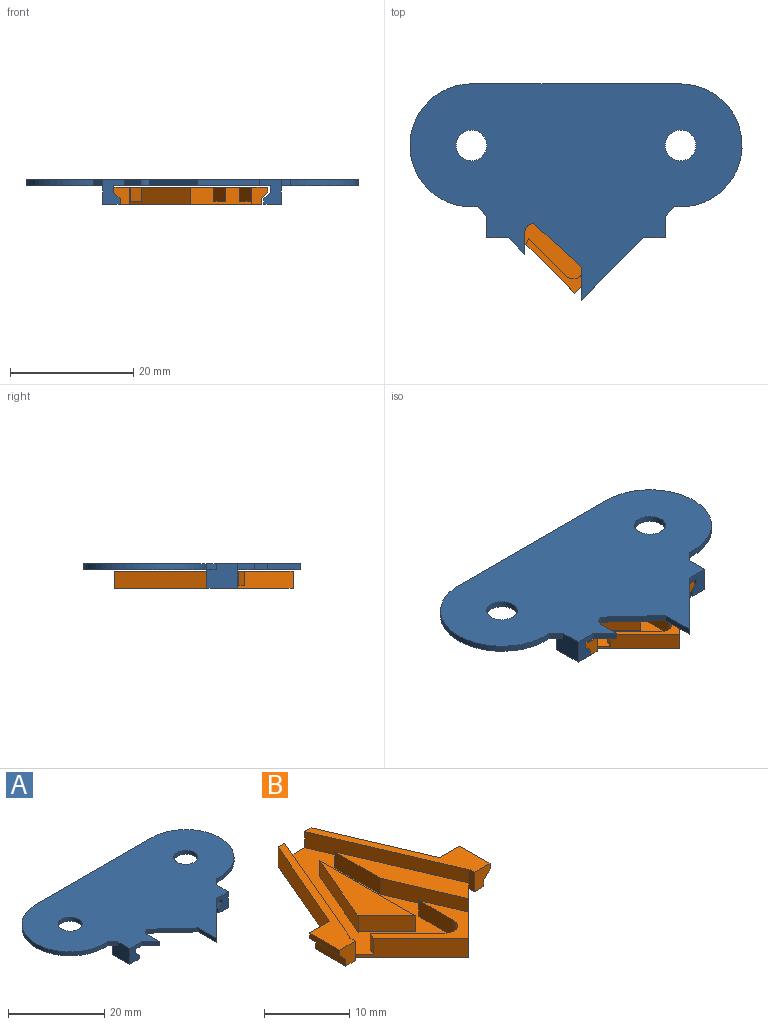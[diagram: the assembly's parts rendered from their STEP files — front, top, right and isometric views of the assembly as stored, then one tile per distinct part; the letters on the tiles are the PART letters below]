
ASSEMBLY  parts=2 mates=1
PART A: 29 faces, bbox 54x35.1x4 mm
  f0: plane 1.54x1.54mm, normal (0.71,-0.71,0), area 2.2mm2, adj f2,f4,f10,f15
  f1: plane 2.69x2.69mm, normal (-0.71,-0.71,0), area 3.8mm2, adj f2,f4,f9,f27
  f2: plane 54x35.14mm, normal (0,0,-1), area 1145.9mm2, adj f0,f1,f3,f5,f6,f7,f8,f9
  f3: plane 1.55x1.55mm, normal (-0.71,-0.71,0), area 2.2mm2, adj f2,f4,f13,f23
  f4: plane 54x35.14mm, normal (0,0,1), area 1163.9mm2, adj f0,f1,f3,f5,f6,f7,f8,f9
  f5: plane 10.14x10.14mm, normal (0.71,-0.71,0), area 14.3mm2, adj f2,f4,f6,f20
  f6: plane 5.36x1mm, normal (-1,0,0), area 5.4mm2, adj f2,f4,f5,f7
  f7: plane 7.7x7.05mm, normal (-0.68,-0.74,0), area 10.4mm2, adj f2,f4,f6,f8
  f8: cylinder r=1.46mm len=1.47mm, axis (0,0,1), area 2.3mm2, adj f2,f4,f7,f9
  f9: plane 3.5x1mm, normal (1,0,0), area 3.5mm2, adj f1,f2,f4,f8
  f10: cylinder r=10mm len=20mm, axis (0,0,1), area 32.4mm2, adj f0,f2,f4,f11
  f11: plane 34.12x1mm, normal (0,1,0), area 34.1mm2, adj f2,f4,f10,f13
  f12: cylinder r=2.5mm len=5mm, axis (0,0,1), area 15.7mm2, adj f2,f4
  f13: cylinder r=10mm len=20mm, axis (0,0,1), area 32.3mm2, adj f2,f3,f4,f11
  f14: cylinder r=2.5mm len=5mm, axis (0,0,1), area 15.7mm2, adj f2,f4
  f15: plane 5x4mm, normal (1,0,0), area 18.5mm2, adj f0,f2,f4,f16,f20,f21
  f16: plane 5x2.8mm, normal (0,0,-1), area 14mm2, adj f15,f17,f20,f21
  f17: plane 5x0.92mm, normal (-1,0,0), area 4.6mm2, adj f16,f18,f20,f21
  f18: plane 5x1mm, normal (-0.71,0,0.71), area 7.1mm2, adj f17,f19,f20,f21
  f19: plane 5x1.08mm, normal (-1,0,0), area 5.4mm2, adj f2,f18,f20,f21
  f20: plane 4x3.5mm, normal (0,-1,0), area 10.3mm2, adj f2,f4,f5,f15,f16,f17,f18,f19
  f21: plane 3x2.8mm, normal (0,1,0), area 6.8mm2, adj f2,f15,f16,f17,f18,f19
  f22: plane 5x2.8mm, normal (0,0,-1), area 14mm2, adj f23,f26,f27,f28
  f23: plane 5x4mm, normal (-1,0,0), area 18.5mm2, adj f2,f3,f4,f22,f27,f28
  f24: plane 5x1.08mm, normal (1,0,0), area 5.4mm2, adj f2,f25,f27,f28
  f25: plane 5x1mm, normal (0.71,0,0.71), area 7.1mm2, adj f24,f26,f27,f28
  f26: plane 5x0.92mm, normal (1,0,0), area 4.6mm2, adj f22,f25,f27,f28
  f27: plane 4x3.5mm, normal (0,-1,0), area 10.3mm2, adj f1,f2,f4,f22,f23,f24,f25,f26
  f28: plane 3x2.8mm, normal (0,1,0), area 6.8mm2, adj f2,f22,f23,f24,f25,f26
PART B: 38 faces, bbox 25x29x2.8 mm
  f0: plane 9.9x9.9mm, normal (-0.71,-0.71,0), area 33mm2, adj f2,f6,f8,f9,f21,f22,f24,f37
  f1: plane 15x6.41mm, normal (0.92,0.39,0), area 45.7mm2, adj f3,f4,f9,f30
  f2: plane 9.9x9.9mm, normal (0.71,-0.71,0), area 26.8mm2, adj f0,f4,f5,f6,f9,f16,f17,f19
  f3: plane 5.5x2.8mm, normal (0,1,0), area 7.8mm2, adj f1,f4,f7,f8,f9,f20,f21,f24
  f4: plane 20x10.84mm, normal (0,0,1), area 33.2mm2, adj f1,f2,f3,f20,f26,f29,f30,f36
  f5: plane 17.95x6.69mm, normal (0,0,1), area 42.4mm2, adj f2,f17,f18,f19
  f6: plane 11.69x9.6mm, normal (0,0,1), area 24.3mm2, adj f0,f2,f13,f14,f15,f16,f22
  f7: plane 15x6.41mm, normal (-0.92,0.39,0), area 45.7mm2, adj f3,f8,f9,f35
  f8: plane 20x10.84mm, normal (0,0,1), area 33.2mm2, adj f0,f3,f7,f21,f32,f34,f35,f37
  f9: plane 29x23mm, normal (0,0,-1), area 373.8mm2, adj f0,f1,f2,f3,f7,f28,f29,f30
  f10: plane 11.29x4.82mm, normal (-0.92,0.39,0), area 28.2mm2, adj f11,f23,f24,f25
  f11: plane 15.99x2.3mm, normal (1,0,0), area 36.8mm2, adj f10,f12,f24,f25
  f12: plane 4.76x4.76mm, normal (-0.71,-0.71,0), area 15.5mm2, adj f11,f23,f24,f25
  f13: plane 6.21x6.21mm, normal (0.71,0.71,0), area 20.2mm2, adj f6,f14,f22,f24
  f14: cylinder r=1.5mm len=2.56mm, axis (0,0,1), area 8.1mm2, adj f6,f13,f15,f24
  f15: plane 5.81x2.3mm, normal (-1,0,0), area 13.4mm2, adj f6,f14,f16,f24
  f16: plane 5.85x2.5mm, normal (0.92,0.39,0), area 14.6mm2, adj f2,f6,f15,f24
  f17: plane 10.31x4.4mm, normal (-0.92,-0.39,0), area 25.8mm2, adj f2,f5,f18,f24
  f18: plane 7.64x2.3mm, normal (-1,0,0), area 17.6mm2, adj f5,f17,f19,f24
  f19: plane 15.66x6.69mm, normal (0.92,0.39,0), area 39.2mm2, adj f2,f5,f18,f24
  f20: plane 19.15x8.18mm, normal (-0.92,-0.39,0), area 47.9mm2, adj f2,f3,f4,f24
  f21: plane 19.15x8.18mm, normal (0.92,-0.39,0), area 47.9mm2, adj f0,f3,f8,f24
  f22: plane 2.3x0.99mm, normal (-0.92,0.39,0), area 2.5mm2, adj f0,f6,f13,f24
  f23: plane 2.3x0.06mm, normal (0.71,-0.71,0), area 0.2mm2, adj f10,f12,f24,f25
  f24: plane 26.71x19.69mm, normal (0,0,1), area 212.4mm2, adj f0,f2,f3,f10,f11,f12,f13,f14
  f25: plane 15.99x4.82mm, normal (0,0,1), area 38.2mm2, adj f10,f11,f12,f23
  f26: plane 5x0.8mm, normal (1,0,0), area 4mm2, adj f4,f27,f29,f30
  f27: plane 5x1mm, normal (0.71,0,-0.71), area 7.1mm2, adj f26,f28,f29,f30
  f28: plane 5x1mm, normal (1,0,0), area 5mm2, adj f9,f27,f29,f30
  f29: plane 2.8x2.6mm, normal (0,-1,0), area 5.8mm2, adj f4,f9,f26,f27,f28,f36
  f30: plane 3.34x2.8mm, normal (0,1,0), area 7.9mm2, adj f1,f4,f9,f26,f27,f28
  f31: plane 5x1mm, normal (-0.71,0,-0.71), area 7.1mm2, adj f32,f33,f34,f35
  f32: plane 5x0.8mm, normal (-1,0,0), area 4mm2, adj f8,f31,f34,f35
  f33: plane 5x1mm, normal (-1,0,0), area 5mm2, adj f9,f31,f34,f35
  f34: plane 2.8x2.6mm, normal (0,-1,0), area 5.8mm2, adj f8,f9,f31,f32,f33,f37
  f35: plane 3.34x2.8mm, normal (0,1,0), area 7.9mm2, adj f7,f8,f9,f31,f32,f33
  f36: plane 2.8x0.9mm, normal (-1,0,0), area 2.5mm2, adj f2,f4,f9,f29
  f37: plane 2.8x0.9mm, normal (1,0,0), area 2.5mm2, adj f0,f8,f9,f34
PLACE A rot(axis=(0,0,-1),0deg) t=(-5.81,33,-8.86)mm
PLACE B t=(-6.01,-16.25,-8.86)mm
MATE fastened A.f26 <-> B.f33  axis (1,0,0) through (-17.51,-2.25,-11.86)mm
